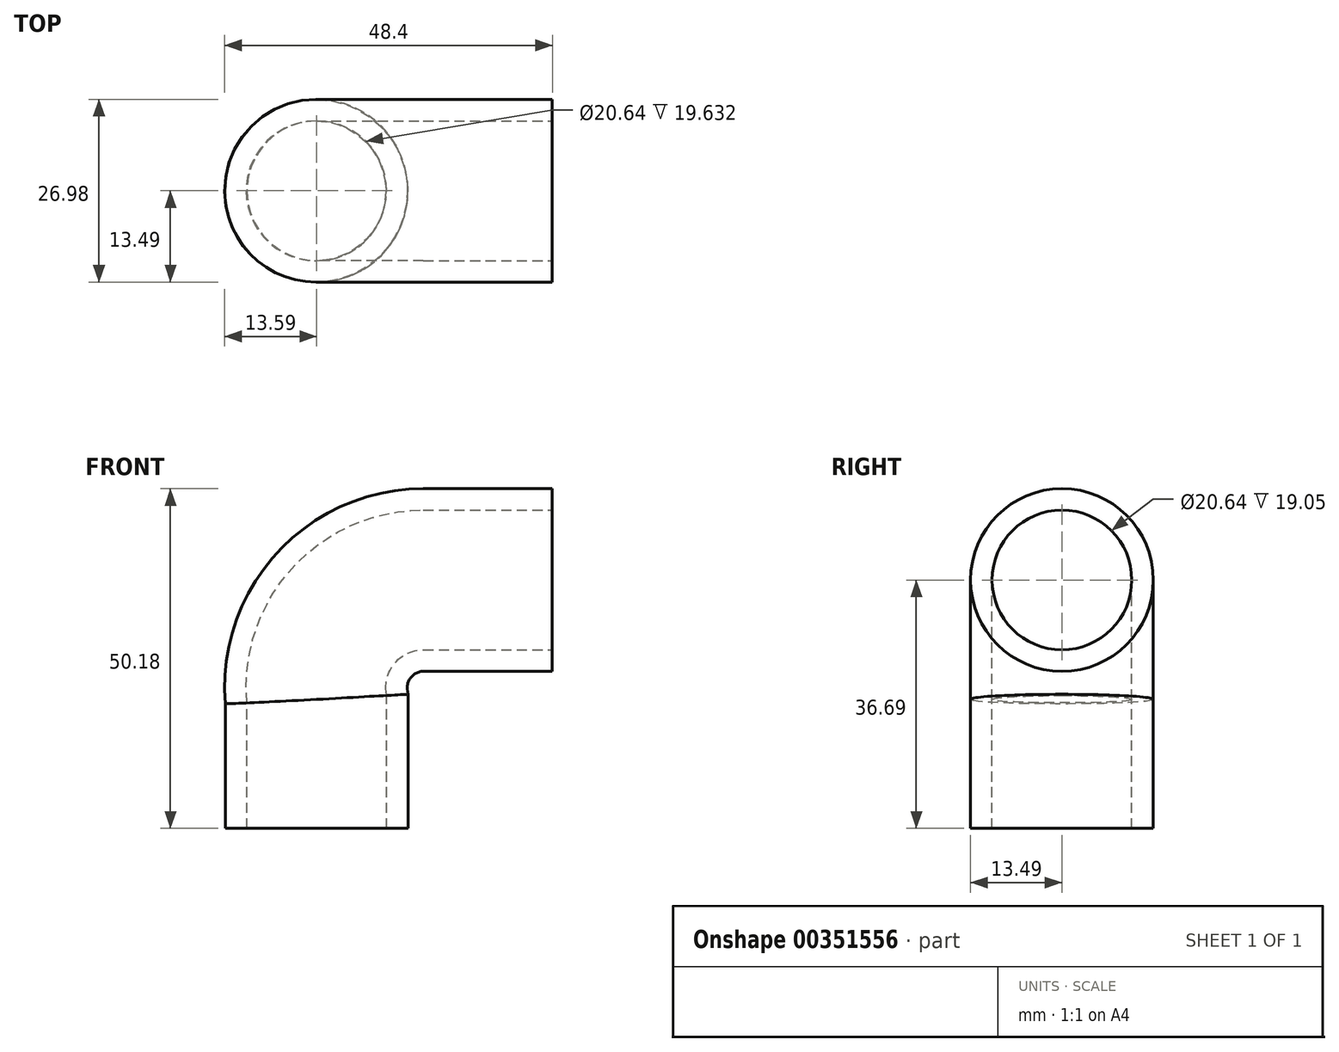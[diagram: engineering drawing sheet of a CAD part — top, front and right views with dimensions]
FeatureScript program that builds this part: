
annotation { "Feature Type Name" : "Feature", "Feature Type Description" : "" }
export const myFeature = defineFeature(function(context is Context, id is Id, definition is map)
    precondition{}
    {
        {
            var Q0;
            Q0=qCreatedBy(makeId("Top.planeOp"),FACE);
            var sketch = newSketch(context, id + "F0", { "sketchPlane" : qUnion([Q0])});
            skCircle(sketch, "E0", {"center": v(0, 0) * mm, "radius": 13.5 * mm});
            skSolve(sketch);
        }
        {
            var Q0;
            Q0=qCreatedBy(makeId("Front.planeOp"),FACE);
            var sketch = newSketch(context, id + "F1", { "sketchPlane" : qUnion([Q0])});
            skLineSegment(sketch, "E1", {"start": v(0, 0) * mm, "end": v(0, 19.05) * mm});
            skLineSegment(sketch, "E2", {"start": v(15.76, 36.7) * mm, "end": v(34.8, 36.7) * mm});
            skArc(sketch, "E3", {"start": v(15.76, 36.7) * mm, "mid": v(3.93, 31.4) * mm, "end": v(0, 19.05) * mm});
            skSolve(sketch);
        }
        {
            var Q0;
            Q0 = qSketchRegion(id + "F0", true);
            var Q1;
            Q1 = qConstructionFilter(qBodyType(qCreatedBy(id + "F1" ,EDGE), BodyType.WIRE), ConstructionObject.NO);
            sweep(context, id + "F2", {"profiles" : qUnion([Q0]), "path" : qUnion([Q1])});
        }
        {
            var Q0;
            Q0=makeQuery(id+"F2.opSweep","CAP_FACE",FACE,{"disambiguationData":[OSD([sQuery(id+"F0.wireOp",EDGE,"E0"),sQuery(id+"F1.wireOp",VERTEX,"E2.end")])],"isStart":false});
            var Q1;
            Q1=makeQuery(id+"F2.opSweep","CAP_FACE",FACE,{"disambiguationData":[OSD([sQuery(id+"F0.wireOp",EDGE,"E0"),sQuery(id+"F1.wireOp",VERTEX,"E1.start")])],"isStart":true});
            shell(context, id + "F3", {"entities" : qUnion([Q0, Q1]), "thickness" : 3.17 * mm});
        }
    });
